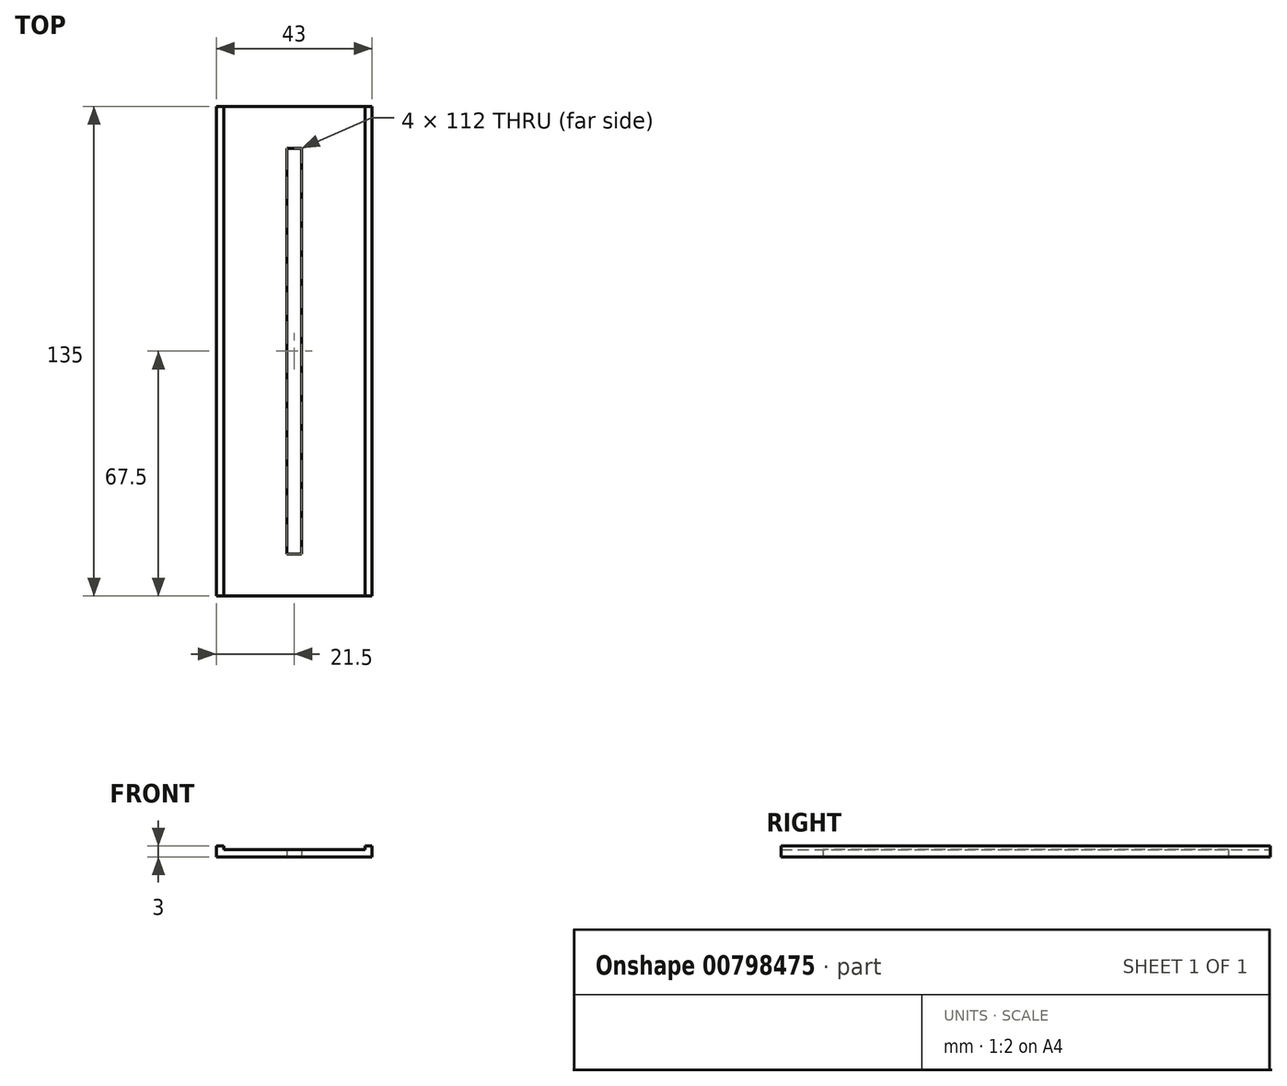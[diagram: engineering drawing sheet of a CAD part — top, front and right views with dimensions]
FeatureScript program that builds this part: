
annotation { "Feature Type Name" : "Feature", "Feature Type Description" : "" }
export const myFeature = defineFeature(function(context is Context, id is Id, definition is map)
    precondition{}
    {
        {
            var Q0;
            Q0=qCreatedBy(makeId("Top.planeOp"),FACE);
            var sketch = newSketch(context, id + "F0", { "sketchPlane" : qUnion([Q0])});
            skLineSegment(sketch, "E0.bottom", {"start": v(-21.5, 67.5) * mm, "end": v(21.5, 67.5) * mm});
            skLineSegment(sketch, "E0.top", {"start": v(-21.5, -67.5) * mm, "end": v(21.5, -67.5) * mm});
            skLineSegment(sketch, "E0.left", {"start": v(-21.5, 67.5) * mm, "end": v(-21.5, -67.5) * mm});
            skLineSegment(sketch, "E0.right", {"start": v(21.5, 67.5) * mm, "end": v(21.5, -67.5) * mm});
            skLineSegment(sketch, "E1.bottom", {"start": v(-2, 56) * mm, "end": v(2, 56) * mm});
            skLineSegment(sketch, "E1.top", {"start": v(-2, -56) * mm, "end": v(2, -56) * mm});
            skLineSegment(sketch, "E1.left", {"start": v(-2, 56) * mm, "end": v(-2, -56) * mm});
            skLineSegment(sketch, "E1.right", {"start": v(2, 56) * mm, "end": v(2, -56) * mm});
            skSolve(sketch);
        }
        {
            var Q0;
            Q0=makeQuery(id+"F0.imprint","IMPRINT",FACE,{"disambiguationData":[TD([[makeQuery(id+"F0.imprint","IMPRINT",EDGE,{"derivedFrom":sQuery(id+"F0.wireOp",EDGE,"E0.bottom")}),-1.0]])]});
            extrude(context, id + "F1", {"entities" : qUnion([Q0]), "depth" : 2 * mm, "offsetDistance" : 25 * mm});
        }
        {
            var Q0;
            Q0=makeQuery(id+"F1.opExtrude","CAP_FACE",FACE,{"disambiguationData":[OSD([sQuery(id+"F0.wireOp",EDGE,"E0.bottom"),sQuery(id+"F0.wireOp",EDGE,"E0.top"),sQuery(id+"F0.wireOp",EDGE,"E0.left"),sQuery(id+"F0.wireOp",EDGE,"E0.right"),sQuery(id+"F0.wireOp",EDGE,"E1.bottom"),sQuery(id+"F0.wireOp",EDGE,"E1.top"),sQuery(id+"F0.wireOp",EDGE,"E1.left"),sQuery(id+"F0.wireOp",EDGE,"E1.right")])],"isStart":false});
            var sketch = newSketch(context, id + "F2", { "sketchPlane" : qUnion([Q0])});
            skLineSegment(sketch, "E2.bottom", {"start": v(-21.5, 67.5) * mm, "end": v(-19.5, 67.5) * mm});
            skLineSegment(sketch, "E2.top", {"start": v(-21.5, -67.5) * mm, "end": v(-19.5, -67.5) * mm});
            skLineSegment(sketch, "E2.left", {"start": v(-21.5, 67.5) * mm, "end": v(-21.5, -67.5) * mm});
            skLineSegment(sketch, "E2.right", {"start": v(-19.5, 67.5) * mm, "end": v(-19.5, -67.5) * mm});
            skLineSegment(sketch, "E3.bottom", {"start": v(21.5, -67.5) * mm, "end": v(19.5, -67.5) * mm});
            skLineSegment(sketch, "E3.top", {"start": v(21.5, 67.5) * mm, "end": v(19.5, 67.5) * mm});
            skLineSegment(sketch, "E3.left", {"start": v(21.5, -67.5) * mm, "end": v(21.5, 67.5) * mm});
            skLineSegment(sketch, "E3.right", {"start": v(19.5, -67.5) * mm, "end": v(19.5, 67.5) * mm});
            skSolve(sketch);
        }
        {
            var Q0;
            Q0=makeQuery(id+"F2.imprint","IMPRINT",FACE,{"disambiguationData":[TD([[makeQuery(id+"F2.imprint","IMPRINT",EDGE,{"derivedFrom":sQuery(id+"F2.wireOp",EDGE,"E2.bottom")}),-1.0]])]});
            var Q1;
            Q1=makeQuery(id+"F2.imprint","IMPRINT",FACE,{"disambiguationData":[TD([[makeQuery(id+"F2.imprint","IMPRINT",EDGE,{"derivedFrom":sQuery(id+"F2.wireOp",EDGE,"E3.bottom")}),1.0]])]});
            extrude(context, id + "F3", {"entities" : qUnion([Q0, Q1]), "operationType" : NewBodyOperationType.ADD, "depth" : 1 * mm, "offsetDistance" : 25 * mm});
        }
    });
